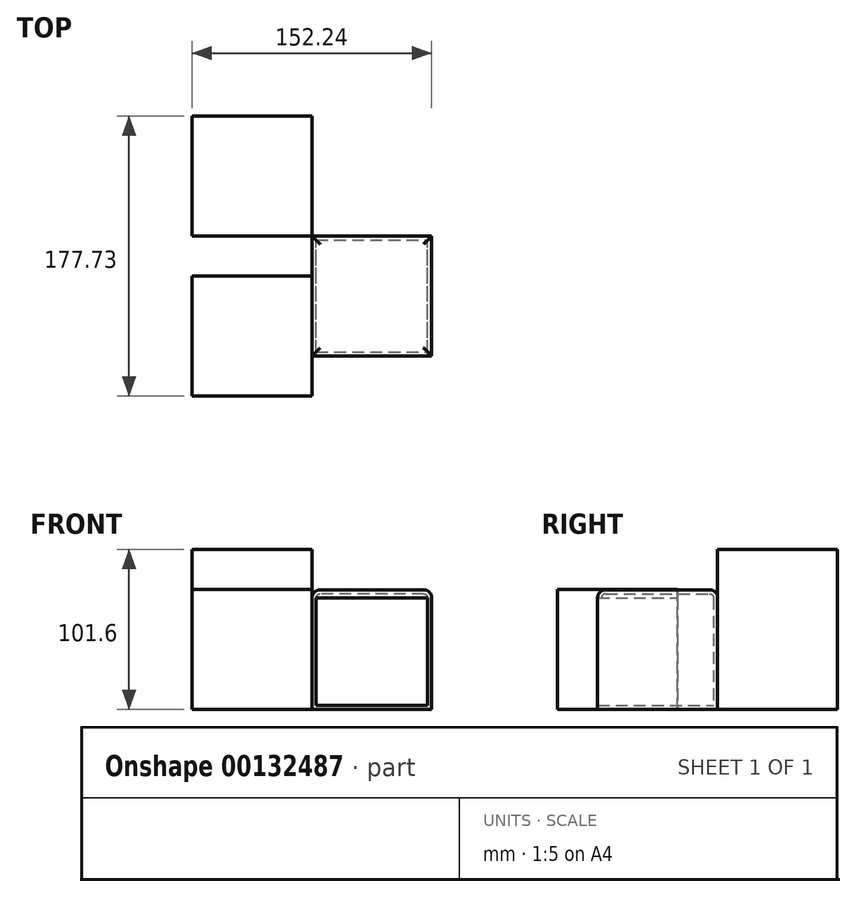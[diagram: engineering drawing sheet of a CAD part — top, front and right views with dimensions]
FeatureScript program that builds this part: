
annotation { "Feature Type Name" : "Feature", "Feature Type Description" : "" }
export const myFeature = defineFeature(function(context is Context, id is Id, definition is map)
    precondition{}
    {
        {
            var Q0;
            Q0=qCreatedBy(makeId("Front.planeOp"),FACE);
            var sketch = newSketch(context, id + "F0", { "sketchPlane" : qUnion([Q0])});
            skLineSegment(sketch, "E0", {"start": v(0, 0) * mm, "end": v(75.95, 0) * mm});
            skLineSegment(sketch, "E1", {"start": v(75.95, 0) * mm, "end": v(75.95, 75.94) * mm});
            skLineSegment(sketch, "E2", {"start": v(75.95, 75.94) * mm, "end": v(0, 75.94) * mm});
            skLineSegment(sketch, "E3", {"start": v(0, 75.94) * mm, "end": v(0, 0) * mm});
            skSolve(sketch);
        }
        {
            var Q0;
            Q0=makeQuery(id+"F0.imprint","IMPRINT",FACE,{"disambiguationData":[TD([[makeQuery(id+"F0.imprint","IMPRINT",EDGE,{"derivedFrom":sQuery(id+"F0.wireOp",EDGE,"E0")}),1.0]])]});
            extrude(context, id + "F1", {"entities" : qUnion([Q0]), "depth" : 76.2 * mm});
        }
        {
            var Q0;
            Q0=qCreatedBy(makeId("Front.planeOp"),FACE);
            cPlane(context, id + "F2", {"entities" : qUnion([Q0]), "cplaneType" : CPlaneType.OFFSET, "offset" : 25.4 * mm, "width" : 152.4 * mm, "height" : 152.4 * mm});
        }
        {
            var Q0;
            Q0=makeQuery(id+"F1.opExtrude","SWEPT_FACE",FACE,{"disambiguationData":[OSD([sQuery(id+"F0.wireOp",EDGE,"E2")])]});
            fillet(context, id + "F3", {"entities" : qUnion([Q0]), "radius" : 5.08 * mm, "tangentPropagation" : true, "allowEdgeOverflow" : false});
        }
        {
            var Q0;
            Q0=makeQuery(id+"F1.opExtrude","CAP_FACE",FACE,{"disambiguationData":[OSD([sQuery(id+"F0.wireOp",EDGE,"E0"),sQuery(id+"F0.wireOp",EDGE,"E1"),sQuery(id+"F0.wireOp",EDGE,"E2"),sQuery(id+"F0.wireOp",EDGE,"E3")])],"isStart":false});
            shell(context, id + "F4", {"entities" : qUnion([Q0]), "thickness" : 2.54 * mm});
        }
        {
            var Q0;
            Q0=qCreatedBy(id+"F2.planeOp",FACE);
            var sketch = newSketch(context, id + "F5", { "sketchPlane" : qUnion([Q0])});
            skLineSegment(sketch, "E4", {"start": v(0, 0) * mm, "end": v(-76.29, 0) * mm});
            skLineSegment(sketch, "E5", {"start": v(-76.29, 0) * mm, "end": v(-76.29, 76.14) * mm});
            skLineSegment(sketch, "E6", {"start": v(-76.29, 76.14) * mm, "end": v(0, 76.14) * mm});
            skLineSegment(sketch, "E7", {"start": v(0, 76.14) * mm, "end": v(0, 0) * mm});
            skSolve(sketch);
        }
        {
            var Q0;
            Q0=makeQuery(id+"F5.imprint","IMPRINT",FACE,{"disambiguationData":[TD([[makeQuery(id+"F5.imprint","IMPRINT",EDGE,{"derivedFrom":sQuery(id+"F5.wireOp",EDGE,"E4")}),-1.0]])]});
            extrude(context, id + "F6", {"entities" : qUnion([Q0]), "operationType" : NewBodyOperationType.ADD, "depth" : 76.2 * mm});
        }
        {
            var Q0;
            Q0=qCreatedBy(makeId("Top.planeOp"),FACE);
            var sketch = newSketch(context, id + "F7", { "sketchPlane" : qUnion([Q0])});
            skLineSegment(sketch, "E8", {"start": v(0, 0) * mm, "end": v(0, 76.13) * mm});
            skLineSegment(sketch, "E9", {"start": v(-76.18, 76.13) * mm, "end": v(-76.18, 0) * mm});
            skLineSegment(sketch, "E10", {"start": v(-76.18, 76.13) * mm, "end": v(0, 76.13) * mm});
            skLineSegment(sketch, "E11", {"start": v(-76.18, 0) * mm, "end": v(0, 0) * mm});
            skSolve(sketch);
        }
        {
            var Q0;
            Q0=makeQuery(id+"F7.imprint","IMPRINT",FACE,{"disambiguationData":[TD([[makeQuery(id+"F7.imprint","IMPRINT",EDGE,{"derivedFrom":sQuery(id+"F7.wireOp",EDGE,"E8")}),1.0]])]});
            extrude(context, id + "F8", {"entities" : qUnion([Q0]), "depth" : 101.6 * mm});
        }
    });
